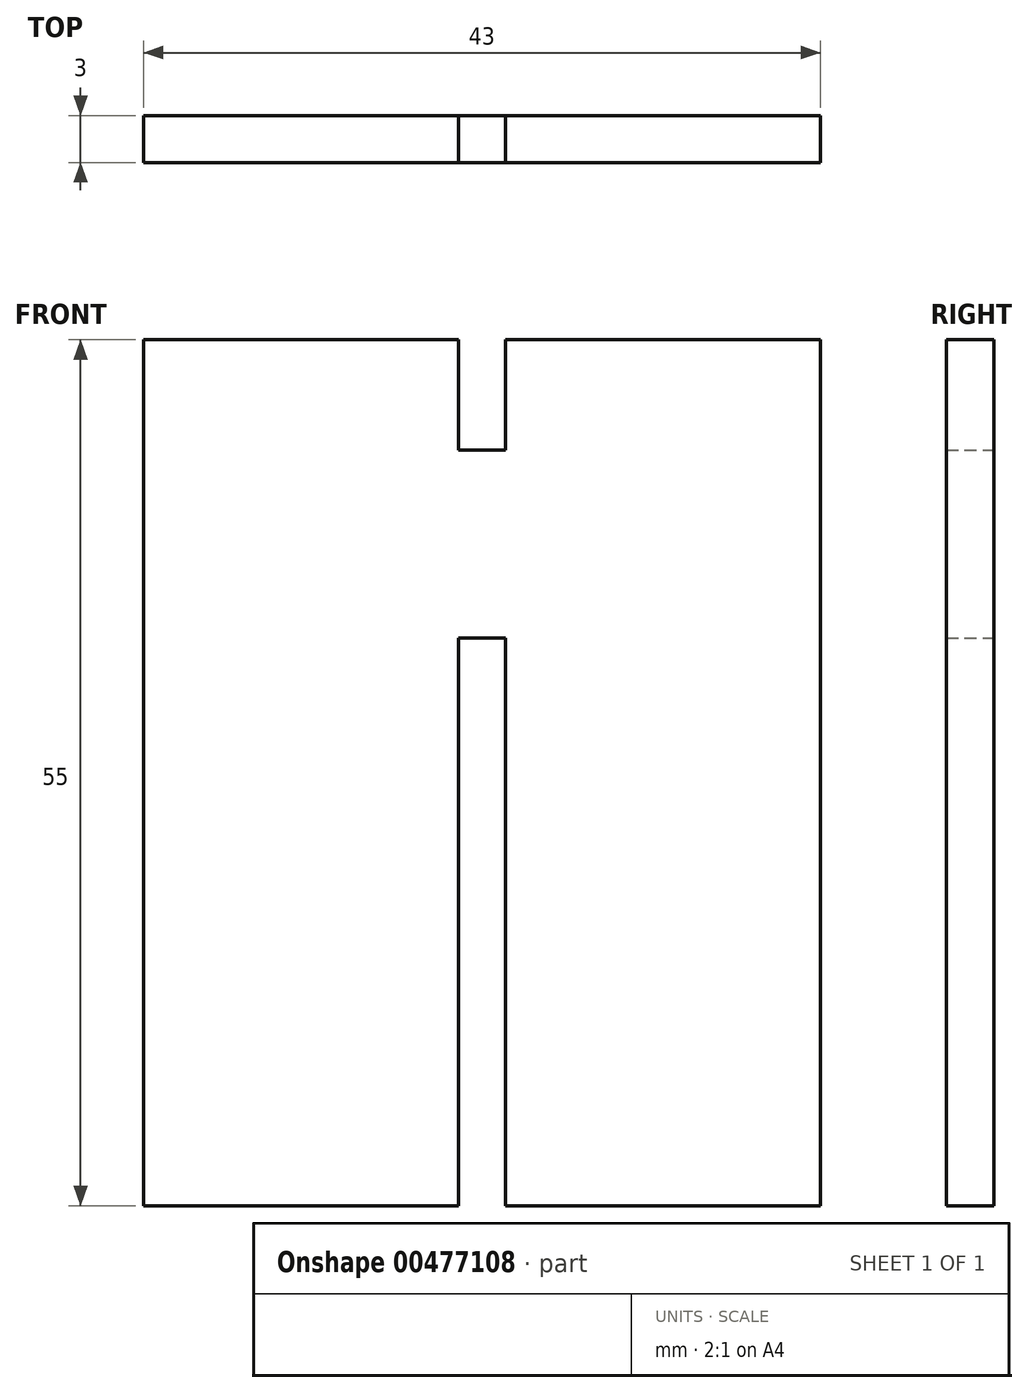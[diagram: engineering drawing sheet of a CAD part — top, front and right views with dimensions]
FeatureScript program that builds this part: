
annotation { "Feature Type Name" : "Feature", "Feature Type Description" : "" }
export const myFeature = defineFeature(function(context is Context, id is Id, definition is map)
    precondition{}
    {
        {
            var Q0;
            Q0=qCreatedBy(makeId("Front.planeOp"),FACE);
            var sketch = newSketch(context, id + "F0", { "sketchPlane" : qUnion([Q0])});
            skLineSegment(sketch, "E0", {"start": v(-32.5, 30.9) * mm, "end": v(-32.5, -24.1) * mm});
            skLineSegment(sketch, "E1", {"start": v(-32.5, -24.1) * mm, "end": v(-12.5, -24.1) * mm});
            skLineSegment(sketch, "E2", {"start": v(-12.5, -24.1) * mm, "end": v(-12.5, 11.95) * mm});
            skLineSegment(sketch, "E3", {"start": v(-12.5, 11.95) * mm, "end": v(-9.5, 11.95) * mm});
            skLineSegment(sketch, "E4", {"start": v(-9.5, 11.95) * mm, "end": v(-9.5, -24.1) * mm});
            skLineSegment(sketch, "E5", {"start": v(-9.5, -24.1) * mm, "end": v(10.5, -24.1) * mm});
            skLineSegment(sketch, "E6", {"start": v(10.5, -24.1) * mm, "end": v(10.5, 30.9) * mm});
            skLineSegment(sketch, "E7", {"start": v(10.5, 30.9) * mm, "end": v(-9.5, 30.9) * mm});
            skLineSegment(sketch, "E8", {"start": v(-9.5, 30.9) * mm, "end": v(-9.5, 23.9) * mm});
            skLineSegment(sketch, "E9", {"start": v(-9.5, 23.9) * mm, "end": v(-12.5, 23.9) * mm});
            skLineSegment(sketch, "E10", {"start": v(-12.5, 23.9) * mm, "end": v(-12.5, 30.9) * mm});
            skLineSegment(sketch, "E11", {"start": v(-12.5, 30.9) * mm, "end": v(-32.5, 30.9) * mm});
            skSolve(sketch);
        }
        {
            var Q0;
            Q0=makeQuery(id+"F0.imprint","IMPRINT",FACE,{"disambiguationData":[TD([[makeQuery(id+"F0.imprint","IMPRINT",EDGE,{"derivedFrom":sQuery(id+"F0.wireOp",EDGE,"E0")}),1.0]])]});
            extrude(context, id + "F1", {"entities" : qUnion([Q0]), "depth" : 3 * mm});
        }
    });
